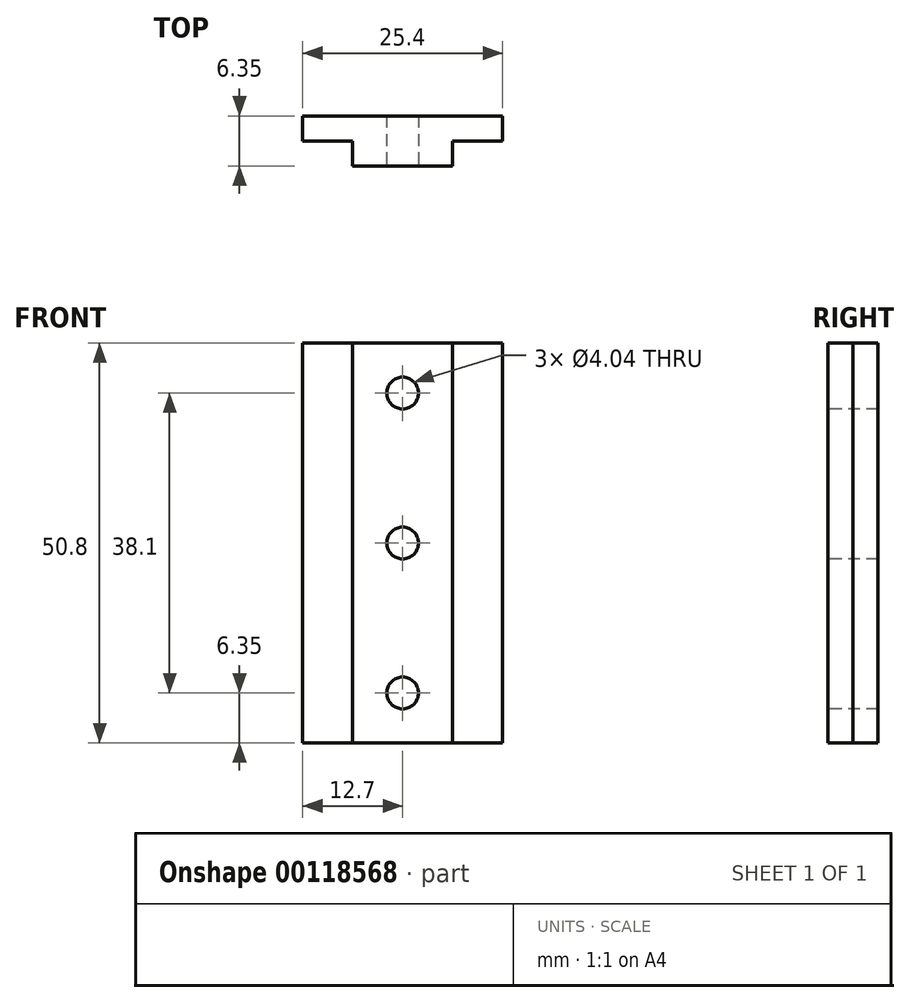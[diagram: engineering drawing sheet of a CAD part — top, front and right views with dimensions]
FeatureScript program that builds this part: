
annotation { "Feature Type Name" : "Feature", "Feature Type Description" : "" }
export const myFeature = defineFeature(function(context is Context, id is Id, definition is map)
    precondition{}
    {
        {
            var Q0;
            Q0=qCreatedBy(makeId("Front.planeOp"),FACE);
            var sketch = newSketch(context, id + "F0", { "sketchPlane" : qUnion([Q0])});
            skLineSegment(sketch, "E0.bottom", {"start": v(12.7, 25.4) * mm, "end": v(-12.7, 25.4) * mm});
            skLineSegment(sketch, "E0.top", {"start": v(12.7, -25.4) * mm, "end": v(-12.7, -25.4) * mm});
            skLineSegment(sketch, "E0.left", {"start": v(12.7, 25.4) * mm, "end": v(12.7, -25.4) * mm});
            skLineSegment(sketch, "E0.right", {"start": v(-12.7, 25.4) * mm, "end": v(-12.7, -25.4) * mm});
            skPoint(sketch, "E0.middle", {"position": v(0, 0) * mm});
            skSolve(sketch);
        }
        {
            var Q0;
            Q0 = qSketchRegion(id + "F0", true);
            extrude(context, id + "F1", {"entities" : qUnion([Q0]), "depth" : 6.35 * mm});
        }
        {
            var Q0;
            Q0=makeQuery(id+"F1.opExtrude","CAP_FACE",FACE,{"disambiguationData":[OSD([sQuery(id+"F0.wireOp",EDGE,"E0.bottom"),sQuery(id+"F0.wireOp",EDGE,"E0.top"),sQuery(id+"F0.wireOp",EDGE,"E0.left"),sQuery(id+"F0.wireOp",EDGE,"E0.right")])],"isStart":false});
            var sketch = newSketch(context, id + "F2", { "sketchPlane" : qUnion([Q0])});
            skLineSegment(sketch, "E1.bottom", {"start": v(6.35, 25.4) * mm, "end": v(-6.35, 25.4) * mm});
            skLineSegment(sketch, "E1.top", {"start": v(6.35, -25.4) * mm, "end": v(-6.35, -25.4) * mm});
            skLineSegment(sketch, "E1.left", {"start": v(6.35, 25.4) * mm, "end": v(6.35, -25.4) * mm});
            skLineSegment(sketch, "E1.right", {"start": v(-6.35, 25.4) * mm, "end": v(-6.35, -25.4) * mm});
            skPoint(sketch, "E1.middle", {"position": v(0, 0) * mm});
            skSolve(sketch);
        }
        {
            var Q0;
            {var subQ0=sQuery(id+"F2.wireOp",EDGE,"E1.right");Q0=makeQuery(id+"F2.imprint","IMPRINT",FACE,{"disambiguationData":[TD([[makeQuery(id+"F2.imprint","IMPRINT",EDGE,{"derivedFrom":subQ0}),-1.0]])]});}
            var Q1;
            {var subQ0=sQuery(id+"F2.wireOp",EDGE,"E1.left");Q1=makeQuery(id+"F2.imprint","IMPRINT",FACE,{"disambiguationData":[TD([[makeQuery(id+"F2.imprint","IMPRINT",EDGE,{"derivedFrom":subQ0}),1.0]])]});}
            extrude(context, id + "F3", {"entities" : qUnion([Q0, Q1]), "operationType" : NewBodyOperationType.REMOVE, "oppositeDirection" : true, "depth" : 3.17 * mm});
        }
        {
            var Q0;
            Q0=makeQuery(id+"F1.opExtrude","CAP_FACE",FACE,{"disambiguationData":[OSD([sQuery(id+"F0.wireOp",EDGE,"E0.bottom"),sQuery(id+"F0.wireOp",EDGE,"E0.top"),sQuery(id+"F0.wireOp",EDGE,"E0.left"),sQuery(id+"F0.wireOp",EDGE,"E0.right")])],"isStart":false});
            var sketch = newSketch(context, id + "F4", { "sketchPlane" : qUnion([Q0])});
            skCircle(sketch, "E2", {"center": v(0, 0) * mm, "radius": 2.02 * mm});
            skCircle(sketch, "E3", {"center": v(0, 19.05) * mm, "radius": 2.02 * mm});
            skCircle(sketch, "E4", {"center": v(0, -19.05) * mm, "radius": 2.02 * mm});
            skSolve(sketch);
        }
        {
            var Q0;
            Q0 = qSketchRegion(id + "F4", true);
            extrude(context, id + "F5", {"entities" : qUnion([Q0]), "operationType" : NewBodyOperationType.REMOVE, "endBound" : BoundingType.THROUGH_ALL, "oppositeDirection" : true, "depth" : 25.4 * mm});
        }
    });
